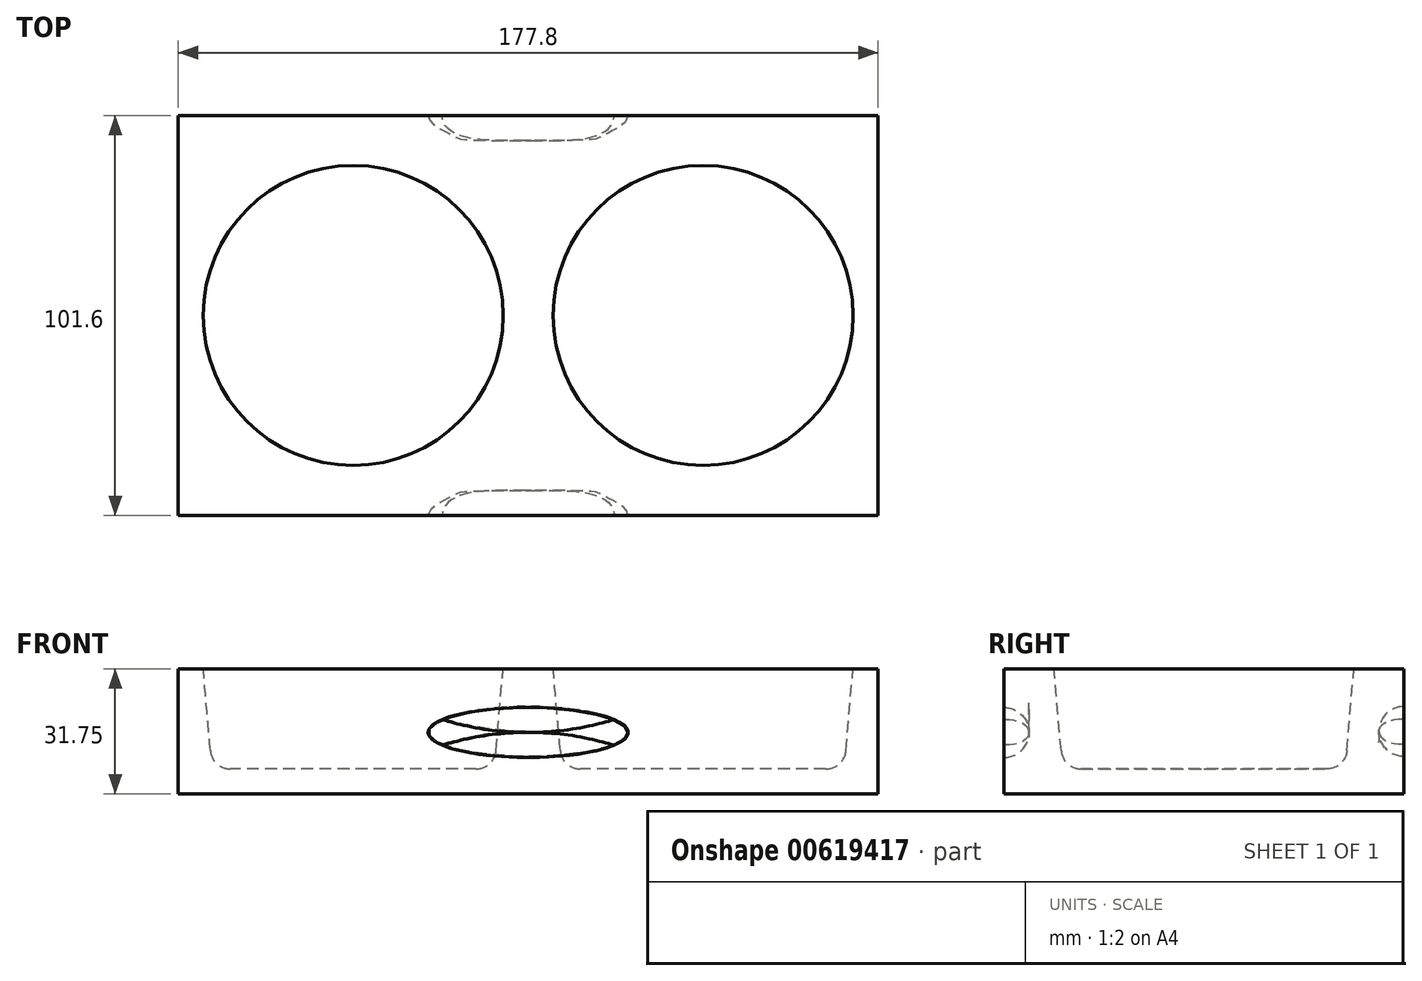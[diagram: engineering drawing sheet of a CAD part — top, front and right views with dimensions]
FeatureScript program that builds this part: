
annotation { "Feature Type Name" : "Feature", "Feature Type Description" : "" }
export const myFeature = defineFeature(function(context is Context, id is Id, definition is map)
    precondition{}
    {
        {
            var Q0;
            Q0=qCreatedBy(makeId("Top.planeOp"),FACE);
            var sketch = newSketch(context, id + "F0", { "sketchPlane" : qUnion([Q0])});
            skLineSegment(sketch, "E0.bottom", {"start": v(88.9, -50.8) * mm, "end": v(-88.9, -50.8) * mm});
            skLineSegment(sketch, "E0.top", {"start": v(88.9, 50.8) * mm, "end": v(-88.9, 50.8) * mm});
            skLineSegment(sketch, "E0.left", {"start": v(88.9, -50.8) * mm, "end": v(88.9, 50.8) * mm});
            skLineSegment(sketch, "E0.right", {"start": v(-88.9, -50.8) * mm, "end": v(-88.9, 50.8) * mm});
            skPoint(sketch, "E0.middle", {"position": v(0, 0) * mm});
            skSolve(sketch);
        }
        {
            var Q0;
            Q0=makeQuery(id+"F0.imprint","IMPRINT",FACE,{"disambiguationData":[TD([[makeQuery(id+"F0.imprint","IMPRINT",EDGE,{"derivedFrom":sQuery(id+"F0.wireOp",EDGE,"E0.bottom")}),-1.0]])]});
            extrude(context, id + "F1", {"entities" : qUnion([Q0]), "depth" : 31.75 * mm, "offsetDistance" : 25.4 * mm});
        }
        {
            var Q0;
            Q0=makeQuery(id+"F1.opExtrude","CAP_FACE",FACE,{"disambiguationData":[OSD([sQuery(id+"F0.wireOp",EDGE,"E0.bottom"),sQuery(id+"F0.wireOp",EDGE,"E0.top"),sQuery(id+"F0.wireOp",EDGE,"E0.left"),sQuery(id+"F0.wireOp",EDGE,"E0.right")])],"isStart":false});
            var sketch = newSketch(context, id + "F2", { "sketchPlane" : qUnion([Q0])});
            skCircle(sketch, "E1", {"center": v(-44.45, 0) * mm, "radius": 38.1 * mm});
            skCircle(sketch, "E2", {"center": v(44.45, 0) * mm, "radius": 38.1 * mm});
            skSolve(sketch);
        }
        {
            var Q0;
            Q0=makeQuery(id+"F2.imprint","IMPRINT",FACE,{"disambiguationData":[TD([[makeQuery(id+"F2.imprint","IMPRINT",EDGE,{"derivedFrom":sQuery(id+"F2.wireOp",EDGE,"E2")}),1.0]])]});
            var Q1;
            Q1=makeQuery(id+"F2.imprint","IMPRINT",FACE,{"disambiguationData":[TD([[makeQuery(id+"F2.imprint","IMPRINT",EDGE,{"derivedFrom":sQuery(id+"F2.wireOp",EDGE,"E1")}),1.0]])]});
            extrude(context, id + "F3", {"entities" : qUnion([Q0, Q1]), "operationType" : NewBodyOperationType.REMOVE, "oppositeDirection" : true, "depth" : 25.4 * mm, "offsetDistance" : 25.4 * mm, "hasDraft" : true, "draftAngle" : 5 * degree, "draftPullDirection" : true});
        }
        {
            var Q0;
            Q0=makeQuery(id+"F3.boolean.opBoolean","COPY",EDGE,{"derivedFrom":makeQuery(id+"F3.opExtrude","CAP_EDGE",EDGE,{"disambiguationData":[OSD([sQuery(id+"F2.wireOp",EDGE,"E1")])],"isStart":false})});
            var Q1;
            Q1=makeQuery(id+"F3.boolean.opBoolean","COPY",EDGE,{"derivedFrom":makeQuery(id+"F3.opExtrude","CAP_EDGE",EDGE,{"disambiguationData":[OSD([sQuery(id+"F2.wireOp",EDGE,"E2")])],"isStart":false})});
            fillet(context, id + "F4", {"entities" : qUnion([Q0, Q1]), "radius" : 5.08 * mm, "tangentPropagation" : true, "allowEdgeOverflow" : false});
        }
        {
            var Q0;
            Q0=makeQuery(id+"F1.opExtrude","SWEPT_FACE",FACE,{"disambiguationData":[OSD([sQuery(id+"F0.wireOp",EDGE,"E0.bottom")])]});
            var sketch = newSketch(context, id + "F5", { "sketchPlane" : qUnion([Q0])});
            skEllipse(sketch, "E3", {"center": v(0, 15.62) * mm, "majorRadius": 25.4 * mm, "minorRadius": 6.35 * mm, "majorAxis": v(1, 0)});
            skSolve(sketch);
        }
        {
            var Q0;
            Q0=makeQuery(id+"F1.opExtrude","SWEPT_FACE",FACE,{"disambiguationData":[OSD([sQuery(id+"F0.wireOp",EDGE,"E0.top")])]});
            var sketch = newSketch(context, id + "F6", { "sketchPlane" : qUnion([Q0])});
            skEllipse(sketch, "E4", {"center": v(0, 15.88) * mm, "majorRadius": 25.4 * mm, "minorRadius": 6.35 * mm, "majorAxis": v(1, 0)});
            skSolve(sketch);
        }
        {
            var Q0;
            Q0=qSketchRegion(id+"F5",true);
            extrude(context, id + "F7", {"entities" : qUnion([Q0]), "operationType" : NewBodyOperationType.REMOVE, "oppositeDirection" : true, "depth" : 6.35 * mm, "offsetDistance" : 25.4 * mm});
        }
        {
            var Q0;
            Q0=qSketchRegion(id+"F6",true);
            extrude(context, id + "F8", {"entities" : qUnion([Q0]), "operationType" : NewBodyOperationType.REMOVE, "oppositeDirection" : true, "depth" : 6.35 * mm, "offsetDistance" : 25.4 * mm});
        }
        {
            var Q0;
            Q0=makeQuery(id+"F8.boolean.opBoolean","COPY",EDGE,{"derivedFrom":makeQuery(id+"F8.opExtrude","CAP_EDGE",EDGE,{"disambiguationData":[OSD([sQuery(id+"F6.wireOp",EDGE,"E4")])],"isStart":false})});
            var Q1;
            Q1=makeQuery(id+"F7.boolean.opBoolean","COPY",EDGE,{"derivedFrom":makeQuery(id+"F7.opExtrude","CAP_EDGE",EDGE,{"disambiguationData":[OSD([sQuery(id+"F5.wireOp",EDGE,"E3")])],"isStart":false})});
            fillet(context, id + "F9", {"entities" : qUnion([Q0, Q1]), "radius" : 6.35 * mm, "tangentPropagation" : true, "allowEdgeOverflow" : false});
        }
    });
